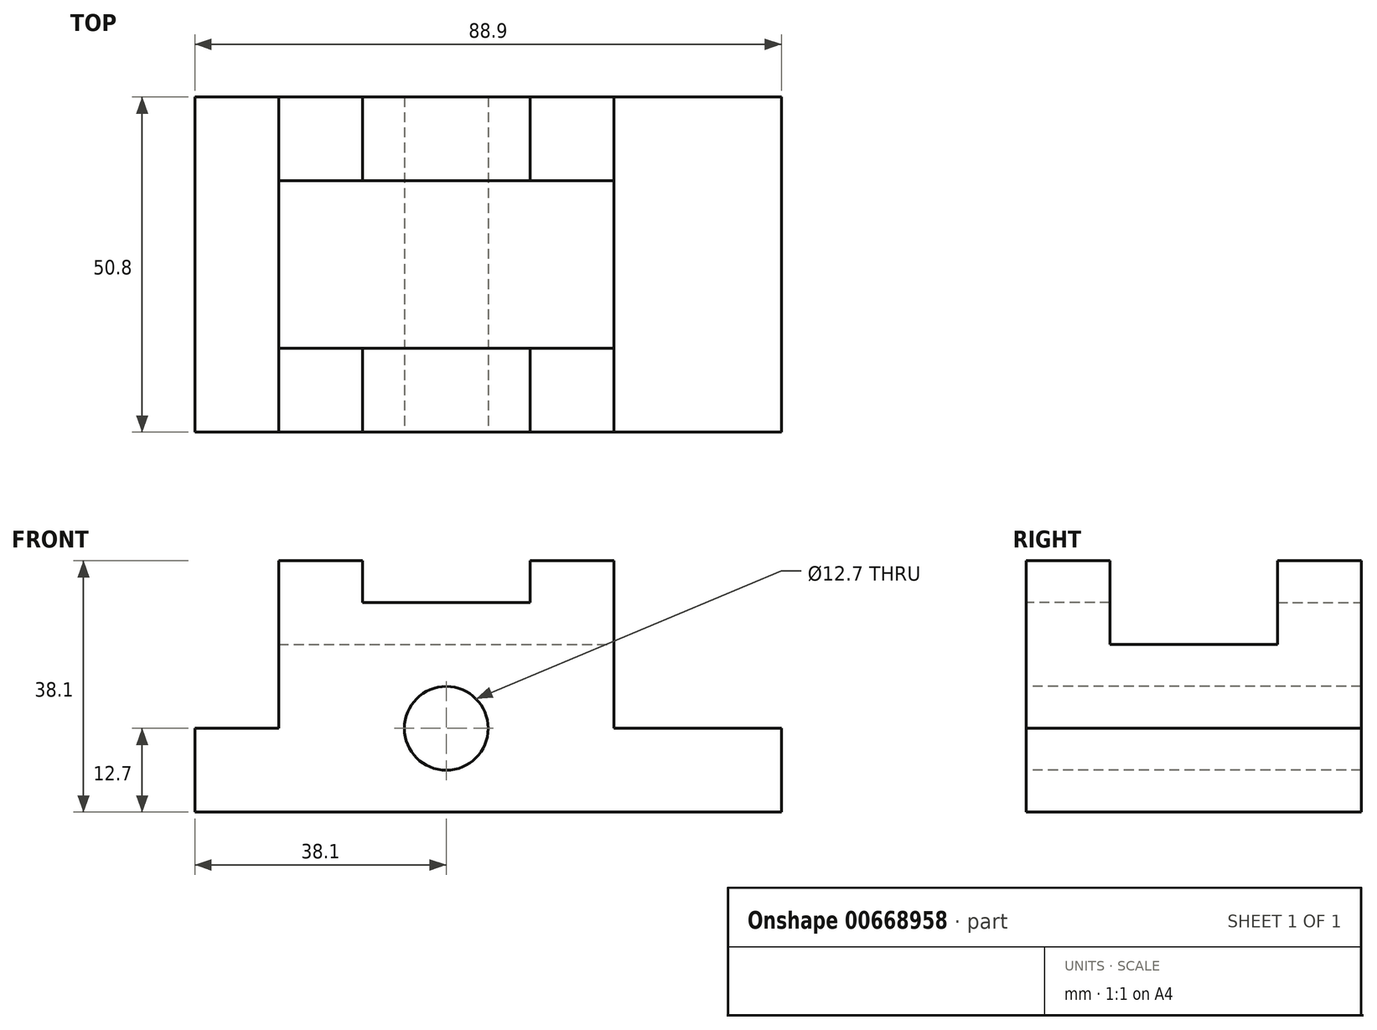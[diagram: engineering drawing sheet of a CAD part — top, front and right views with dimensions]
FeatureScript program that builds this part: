
annotation { "Feature Type Name" : "Feature", "Feature Type Description" : "" }
export const myFeature = defineFeature(function(context is Context, id is Id, definition is map)
    precondition{}
    {
        {
            var Q0;
            Q0=qCreatedBy(makeId("Front.planeOp"),FACE);
            var sketch = newSketch(context, id + "F0", { "sketchPlane" : qUnion([Q0])});
            skLineSegment(sketch, "E0.bottom", {"start": v(-44.45, 19.05) * mm, "end": v(44.45, 19.05) * mm});
            skLineSegment(sketch, "E0.top", {"start": v(-44.45, -19.05) * mm, "end": v(44.45, -19.05) * mm});
            skLineSegment(sketch, "E0.left", {"start": v(-44.45, 19.05) * mm, "end": v(-44.45, -19.05) * mm});
            skLineSegment(sketch, "E0.right", {"start": v(44.45, 19.05) * mm, "end": v(44.45, -19.05) * mm});
            skPoint(sketch, "E0.middle", {"position": v(0, 0) * mm});
            skSolve(sketch);
        }
        {
            var Q0;
            Q0 = qSketchRegion(id + "F0", true);
            extrude(context, id + "F1", {"entities" : qUnion([Q0]), "depth" : 50.8 * mm, "offsetDistance" : 25.4 * mm});
        }
        {
            var Q0;
            Q0=makeQuery(id+"F1.opExtrude","SWEPT_FACE",FACE,{"disambiguationData":[OSD([sQuery(id+"F0.wireOp",EDGE,"E0.bottom")])]});
            var sketch = newSketch(context, id + "F2", { "sketchPlane" : qUnion([Q0])});
            skLineSegment(sketch, "E1.bottom", {"start": v(-44.45, 0) * mm, "end": v(-31.75, 0) * mm});
            skLineSegment(sketch, "E1.top", {"start": v(-44.45, -50.8) * mm, "end": v(-31.75, -50.8) * mm});
            skLineSegment(sketch, "E1.left", {"start": v(-44.45, 0) * mm, "end": v(-44.45, -50.8) * mm});
            skLineSegment(sketch, "E1.right", {"start": v(-31.75, 0) * mm, "end": v(-31.75, -50.8) * mm});
            skSolve(sketch);
        }
        {
            var Q0;
            Q0 = qSketchRegion(id + "F2", true);
            extrude(context, id + "F3", {"entities" : qUnion([Q0]), "operationType" : NewBodyOperationType.REMOVE, "oppositeDirection" : true, "depth" : 25.4 * mm, "offsetDistance" : 25.4 * mm});
        }
        {
            var Q0;
            Q0=makeQuery(id+"F1.opExtrude","SWEPT_FACE",FACE,{"disambiguationData":[OSD([sQuery(id+"F0.wireOp",EDGE,"E0.bottom")])]});
            var sketch = newSketch(context, id + "F4", { "sketchPlane" : qUnion([Q0])});
            skLineSegment(sketch, "E2.bottom", {"start": v(44.45, 0) * mm, "end": v(19.05, 0) * mm});
            skLineSegment(sketch, "E2.top", {"start": v(44.45, -50.8) * mm, "end": v(19.05, -50.8) * mm});
            skLineSegment(sketch, "E2.left", {"start": v(44.45, 0) * mm, "end": v(44.45, -50.8) * mm});
            skLineSegment(sketch, "E2.right", {"start": v(19.05, 0) * mm, "end": v(19.05, -50.8) * mm});
            skSolve(sketch);
        }
        {
            var Q0;
            Q0=makeQuery(id+"F4.imprint","IMPRINT",FACE,{"disambiguationData":[TD([[makeQuery(id+"F4.imprint","IMPRINT",EDGE,{"derivedFrom":sQuery(id+"F4.wireOp",EDGE,"E2.bottom")}),-1.0]])]});
            extrude(context, id + "F5", {"entities" : qUnion([Q0]), "operationType" : NewBodyOperationType.REMOVE, "oppositeDirection" : true, "depth" : 25.4 * mm, "offsetDistance" : 25.4 * mm});
        }
        {
            var Q0;
            Q0=makeQuery(id+"F1.opExtrude","CAP_FACE",FACE,{"disambiguationData":[OSD([sQuery(id+"F0.wireOp",EDGE,"E0.bottom"),sQuery(id+"F0.wireOp",EDGE,"E0.top"),sQuery(id+"F0.wireOp",EDGE,"E0.left"),sQuery(id+"F0.wireOp",EDGE,"E0.right")])],"isStart":false});
            var sketch = newSketch(context, id + "F6", { "sketchPlane" : qUnion([Q0])});
            skCircle(sketch, "E3", {"center": v(-6.35, -6.35) * mm, "radius": 6.35 * mm});
            skPoint(sketch, "E3.first.point", {"position": v(-6.35, 0) * mm});
            skPoint(sketch, "E3.second.point", {"position": v(0, -6.35) * mm});
            skPoint(sketch, "E3.third.point", {"position": v(-8.26, -12.4) * mm});
            skSolve(sketch);
        }
        {
            var Q0;
            Q0 = qSketchRegion(id + "F6", true);
            extrude(context, id + "F7", {"entities" : qUnion([Q0]), "operationType" : NewBodyOperationType.REMOVE, "endBound" : BoundingType.THROUGH_ALL, "oppositeDirection" : true, "depth" : 25.4 * mm, "offsetDistance" : 25.4 * mm});
        }
        {
            var Q0;
            Q0=makeQuery(id+"F5.boolean.opBoolean","COPY",FACE,{"derivedFrom":makeQuery(id+"F5.opExtrude","SWEPT_FACE",FACE,{"disambiguationData":[OSD([sQuery(id+"F4.wireOp",EDGE,"E2.right")])]})});
            var sketch = newSketch(context, id + "F8", { "sketchPlane" : qUnion([Q0])});
            skLineSegment(sketch, "E4.bottom", {"start": v(-38.1, 19.05) * mm, "end": v(-12.7, 19.05) * mm});
            skLineSegment(sketch, "E4.top", {"start": v(-38.1, 6.35) * mm, "end": v(-12.7, 6.35) * mm});
            skLineSegment(sketch, "E4.left", {"start": v(-38.1, 19.05) * mm, "end": v(-38.1, 6.35) * mm});
            skLineSegment(sketch, "E4.right", {"start": v(-12.7, 19.05) * mm, "end": v(-12.7, 6.35) * mm});
            skSolve(sketch);
        }
        {
            var Q0;
            Q0 = qSketchRegion(id + "F8", true);
            extrude(context, id + "F9", {"entities" : qUnion([Q0]), "operationType" : NewBodyOperationType.REMOVE, "endBound" : BoundingType.THROUGH_ALL, "oppositeDirection" : true, "depth" : 25.4 * mm, "offsetDistance" : 25.4 * mm});
        }
        {
            var Q0;
            Q0=makeQuery(id+"F1.opExtrude","CAP_FACE",FACE,{"disambiguationData":[OSD([sQuery(id+"F0.wireOp",EDGE,"E0.bottom"),sQuery(id+"F0.wireOp",EDGE,"E0.top"),sQuery(id+"F0.wireOp",EDGE,"E0.left"),sQuery(id+"F0.wireOp",EDGE,"E0.right")])],"isStart":false});
            var sketch = newSketch(context, id + "F10", { "sketchPlane" : qUnion([Q0])});
            skLineSegment(sketch, "E5.bottom", {"start": v(-19.05, 19.05) * mm, "end": v(6.35, 19.05) * mm});
            skLineSegment(sketch, "E5.top", {"start": v(-19.05, 12.7) * mm, "end": v(6.35, 12.7) * mm});
            skLineSegment(sketch, "E5.left", {"start": v(-19.05, 19.05) * mm, "end": v(-19.05, 12.7) * mm});
            skLineSegment(sketch, "E5.right", {"start": v(6.35, 19.05) * mm, "end": v(6.35, 12.7) * mm});
            skSolve(sketch);
        }
        {
            var Q0;
            Q0 = qSketchRegion(id + "F10", true);
            extrude(context, id + "F11", {"entities" : qUnion([Q0]), "operationType" : NewBodyOperationType.REMOVE, "oppositeDirection" : true, "depth" : 12.7 * mm, "offsetDistance" : 25.4 * mm});
        }
        {
            var Q0;
            Q0=makeQuery(id+"F1.opExtrude","CAP_FACE",FACE,{"disambiguationData":[OSD([sQuery(id+"F0.wireOp",EDGE,"E0.bottom"),sQuery(id+"F0.wireOp",EDGE,"E0.top"),sQuery(id+"F0.wireOp",EDGE,"E0.left"),sQuery(id+"F0.wireOp",EDGE,"E0.right")])],"isStart":true});
            var sketch = newSketch(context, id + "F12", { "sketchPlane" : qUnion([Q0])});
            skLineSegment(sketch, "E6.bottom", {"start": v(-6.35, 19.05) * mm, "end": v(19.05, 19.05) * mm});
            skLineSegment(sketch, "E6.top", {"start": v(-6.35, 12.7) * mm, "end": v(19.05, 12.7) * mm});
            skLineSegment(sketch, "E6.left", {"start": v(-6.35, 19.05) * mm, "end": v(-6.35, 12.7) * mm});
            skLineSegment(sketch, "E6.right", {"start": v(19.05, 19.05) * mm, "end": v(19.05, 12.7) * mm});
            skSolve(sketch);
        }
        {
            var Q0;
            Q0 = qSketchRegion(id + "F12", true);
            extrude(context, id + "F13", {"entities" : qUnion([Q0]), "operationType" : NewBodyOperationType.REMOVE, "oppositeDirection" : true, "depth" : 12.7 * mm, "offsetDistance" : 25.4 * mm});
        }
    });
